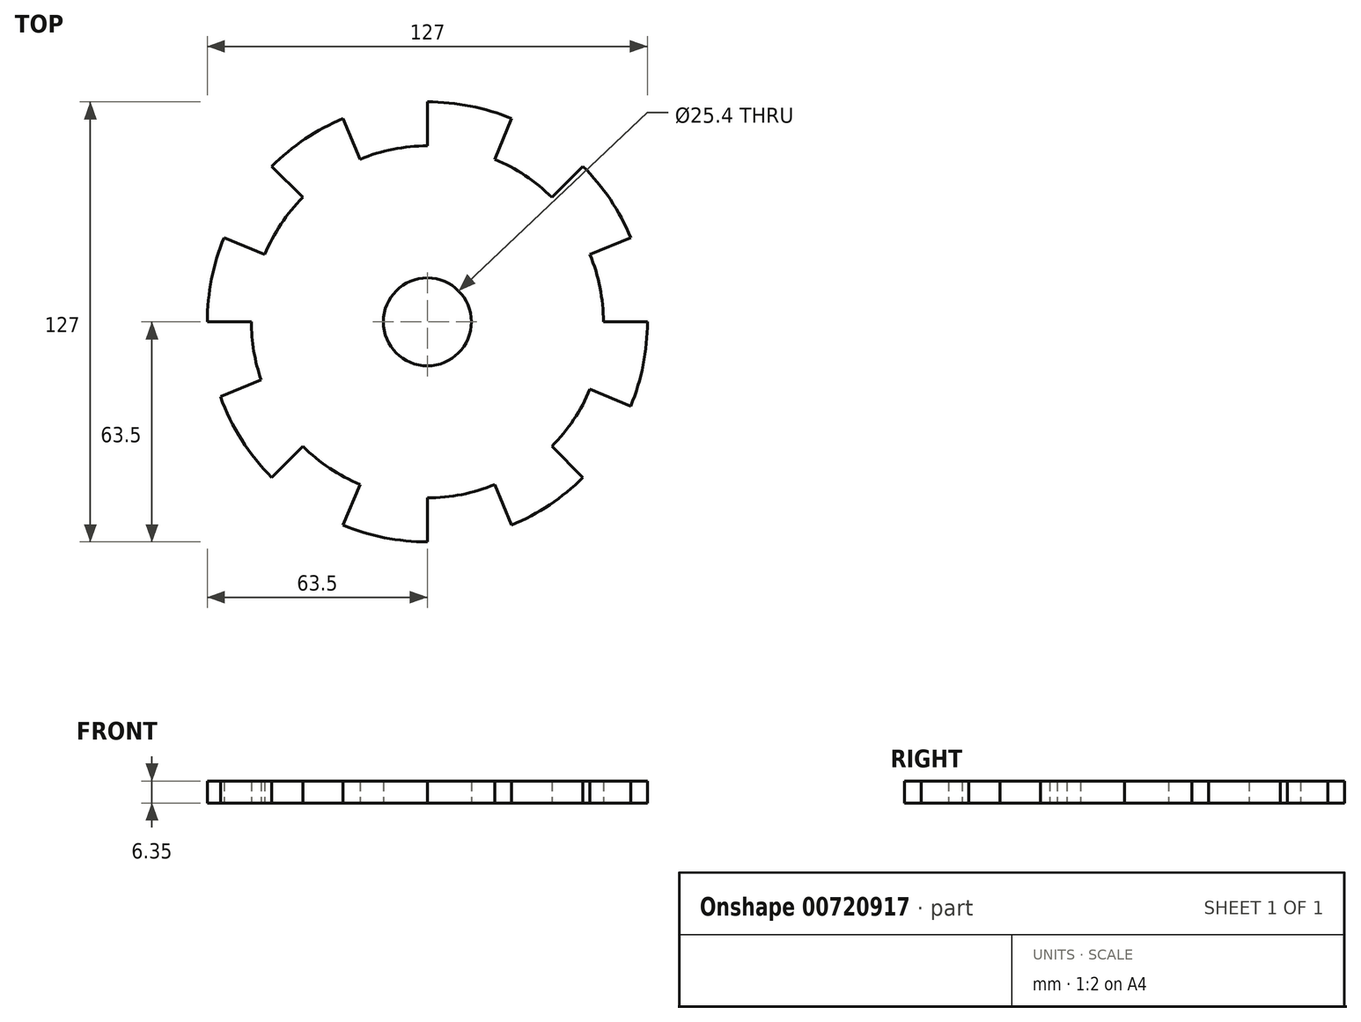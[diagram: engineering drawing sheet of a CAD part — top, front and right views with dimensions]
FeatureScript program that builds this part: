
annotation { "Feature Type Name" : "Feature", "Feature Type Description" : "" }
export const myFeature = defineFeature(function(context is Context, id is Id, definition is map)
    precondition{}
    {
        {
            var Q0;
            Q0=qCreatedBy(makeId("Top.planeOp"),FACE);
            var sketch = newSketch(context, id + "F0", { "sketchPlane" : qUnion([Q0])});
            skArc(sketch, "E0", {"start": v(-58.67, 24.3) * mm, "mid": v(-62.28, 12.39) * mm, "end": v(-63.5, 0) * mm});
            skCircle(sketch, "E1", {"center": v(0, 0) * mm, "radius": 12.7 * mm});
            skLineSegment(sketch, "E2", {"start": v(-63.5, 0) * mm, "end": v(-50.8, 0) * mm});
            skLineSegment(sketch, "E3.1.0", {"start": v(-59.72, -21.57) * mm, "end": v(-47.97, -16.7) * mm});
            skLineSegment(sketch, "E3.2.0", {"start": v(-44.9, -44.9) * mm, "end": v(-35.92, -35.92) * mm});
            skLineSegment(sketch, "E3.3.0", {"start": v(-24.3, -58.67) * mm, "end": v(-19.44, -46.93) * mm});
            skLineSegment(sketch, "E3.4.0", {"start": v(0, -63.5) * mm, "end": v(0, -50.8) * mm});
            skLineSegment(sketch, "E3.5.0", {"start": v(24.3, -58.67) * mm, "end": v(19.44, -46.93) * mm});
            skLineSegment(sketch, "E3.6.0", {"start": v(44.9, -44.9) * mm, "end": v(35.92, -35.92) * mm});
            skLineSegment(sketch, "E3.7.0", {"start": v(58.67, -24.3) * mm, "end": v(46.93, -19.44) * mm});
            skLineSegment(sketch, "E3.8.0", {"start": v(63.5, 0) * mm, "end": v(50.8, 0) * mm});
            skLineSegment(sketch, "E3.9.0", {"start": v(58.67, 24.3) * mm, "end": v(46.93, 19.44) * mm});
            skLineSegment(sketch, "E3.10.0", {"start": v(44.9, 44.9) * mm, "end": v(35.92, 35.92) * mm});
            skLineSegment(sketch, "E3.11.0", {"start": v(24.3, 58.67) * mm, "end": v(19.44, 46.93) * mm});
            skLineSegment(sketch, "E3.12.0", {"start": v(0, 63.5) * mm, "end": v(0, 50.8) * mm});
            skLineSegment(sketch, "E3.13.0", {"start": v(-24.3, 58.67) * mm, "end": v(-19.44, 46.93) * mm});
            skLineSegment(sketch, "E3.14.0", {"start": v(-44.9, 44.9) * mm, "end": v(-35.92, 35.92) * mm});
            skLineSegment(sketch, "E3.15.0", {"start": v(-58.67, 24.3) * mm, "end": v(-46.93, 19.44) * mm});
            skArc(sketch, "E4", {"start": v(-50.8, 0) * mm, "mid": v(-50.09, -8.47) * mm, "end": v(-47.97, -16.7) * mm});
            skArc(sketch, "E5.trimOffspring", {"start": v(-24.3, 58.67) * mm, "mid": v(-35.28, 52.8) * mm, "end": v(-44.9, 44.9) * mm});
            skArc(sketch, "E6.trimOffspring", {"start": v(24.3, 58.67) * mm, "mid": v(12.39, 62.28) * mm, "end": v(0, 63.5) * mm});
            skArc(sketch, "E7.trimOffspring", {"start": v(58.67, 24.3) * mm, "mid": v(52.8, 35.28) * mm, "end": v(44.9, 44.9) * mm});
            skArc(sketch, "E8.trimOffspring", {"start": v(58.67, -24.3) * mm, "mid": v(62.28, -12.39) * mm, "end": v(63.5, 0) * mm});
            skArc(sketch, "E9.trimOffspring", {"start": v(24.3, -58.67) * mm, "mid": v(35.28, -52.8) * mm, "end": v(44.9, -44.9) * mm});
            skArc(sketch, "E10.trimOffspring", {"start": v(-24.3, -58.67) * mm, "mid": v(-12.39, -62.28) * mm, "end": v(0, -63.5) * mm});
            skArc(sketch, "E11.trimOffspring", {"start": v(-59.72, -21.57) * mm, "mid": v(-53.6, -34.05) * mm, "end": v(-44.9, -44.9) * mm});
            skArc(sketch, "E12.trimOffspring", {"start": v(-35.92, 35.92) * mm, "mid": v(-42.24, 28.22) * mm, "end": v(-46.93, 19.44) * mm});
            skArc(sketch, "E13.trimOffspring", {"start": v(0, 50.8) * mm, "mid": v(-9.91, 49.82) * mm, "end": v(-19.44, 46.93) * mm});
            skArc(sketch, "E14.trimOffspring", {"start": v(35.92, 35.92) * mm, "mid": v(28.22, 42.24) * mm, "end": v(19.44, 46.93) * mm});
            skArc(sketch, "E15.trimOffspring", {"start": v(50.8, 0) * mm, "mid": v(49.82, 9.91) * mm, "end": v(46.93, 19.44) * mm});
            skArc(sketch, "E16.trimOffspring", {"start": v(35.92, -35.92) * mm, "mid": v(42.24, -28.22) * mm, "end": v(46.93, -19.44) * mm});
            skArc(sketch, "E17.trimOffspring", {"start": v(0, -50.8) * mm, "mid": v(9.91, -49.82) * mm, "end": v(19.44, -46.93) * mm});
            skArc(sketch, "E18.trimOffspring", {"start": v(-35.92, -35.92) * mm, "mid": v(-28.22, -42.24) * mm, "end": v(-19.44, -46.93) * mm});
            skSolve(sketch);
        }
        {
            var Q0;
            Q0=makeQuery(id+"F0.imprint","IMPRINT",FACE,{"disambiguationData":[TD([[makeQuery(id+"F0.imprint","IMPRINT",EDGE,{"derivedFrom":sQuery(id+"F0.wireOp",EDGE,"E0")}),1.0]])]});
            extrude(context, id + "F1", {"entities" : qUnion([Q0]), "depth" : 6.35 * mm, "offsetDistance" : 25.4 * mm});
        }
    });
